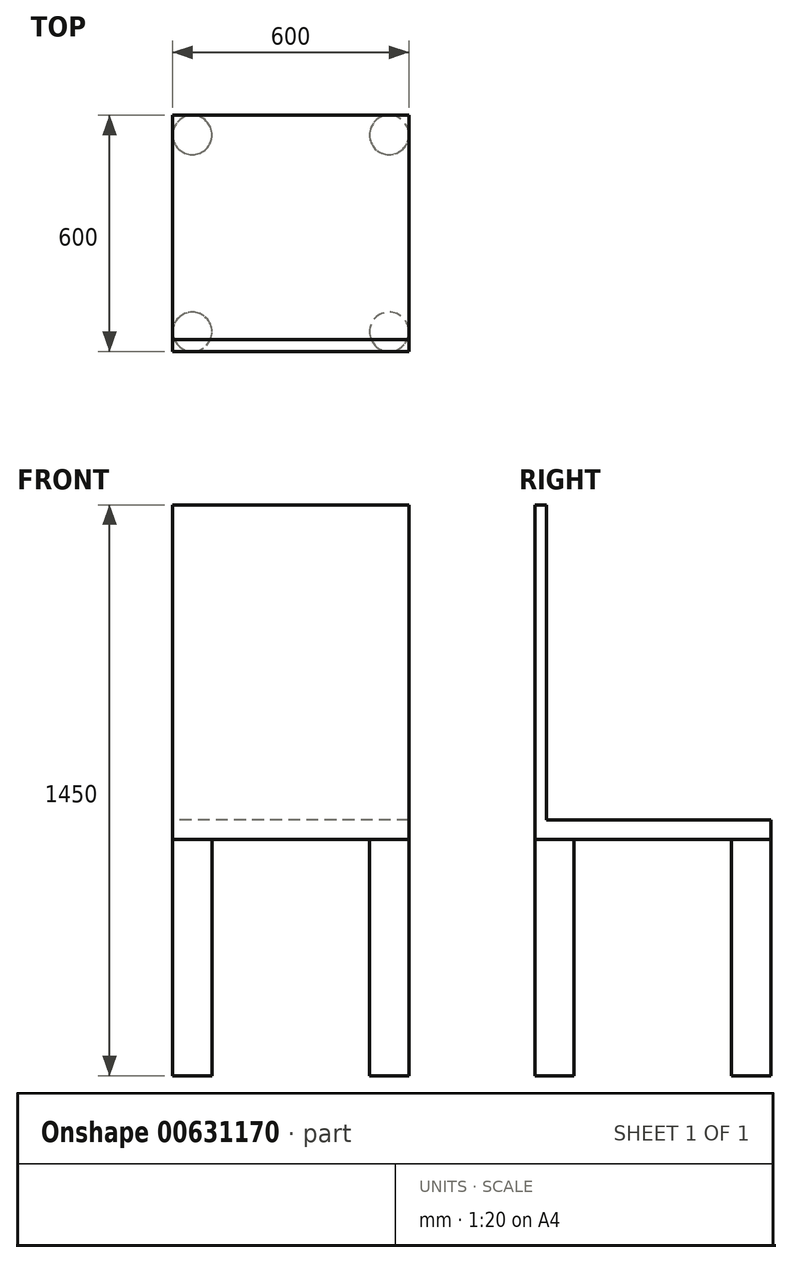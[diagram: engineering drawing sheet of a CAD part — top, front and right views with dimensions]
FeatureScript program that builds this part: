
annotation { "Feature Type Name" : "Feature", "Feature Type Description" : "" }
export const myFeature = defineFeature(function(context is Context, id is Id, definition is map)
    precondition{}
    {
        {
            var Q0;
            Q0=qCreatedBy(makeId("Top.planeOp"),FACE);
            var sketch = newSketch(context, id + "F0", { "sketchPlane" : qUnion([Q0])});
            skLineSegment(sketch, "E0.bottom", {"start": v(300, 300) * mm, "end": v(-300, 300) * mm});
            skLineSegment(sketch, "E0.top", {"start": v(300, -300) * mm, "end": v(-300, -300) * mm});
            skLineSegment(sketch, "E0.left", {"start": v(300, 300) * mm, "end": v(300, -300) * mm});
            skLineSegment(sketch, "E0.right", {"start": v(-300, 300) * mm, "end": v(-300, -300) * mm});
            skPoint(sketch, "E0.middle", {"position": v(0, 0) * mm});
            skSolve(sketch);
        }
        {
            var Q0;
            Q0=makeQuery(id+"F0.imprint","IMPRINT",FACE,{"disambiguationData":[TD([[makeQuery(id+"F0.imprint","IMPRINT",EDGE,{"derivedFrom":sQuery(id+"F0.wireOp",EDGE,"E0.bottom")}),1.0]])]});
            extrude(context, id + "F1", {"entities" : qUnion([Q0]), "depth" : 50 * mm, "offsetDistance" : 25.4 * mm});
        }
        {
            var Q0;
            Q0=makeQuery(id+"F1.opExtrude","CAP_FACE",FACE,{"disambiguationData":[OSD([sQuery(id+"F0.wireOp",EDGE,"E0.bottom"),sQuery(id+"F0.wireOp",EDGE,"E0.top"),sQuery(id+"F0.wireOp",EDGE,"E0.left"),sQuery(id+"F0.wireOp",EDGE,"E0.right")])],"isStart":false});
            var sketch = newSketch(context, id + "F2", { "sketchPlane" : qUnion([Q0])});
            skLineSegment(sketch, "E1.bottom", {"start": v(300, -300) * mm, "end": v(-300, -300) * mm});
            skLineSegment(sketch, "E1.top", {"start": v(300, -270) * mm, "end": v(-300, -270) * mm});
            skLineSegment(sketch, "E1.left", {"start": v(300, -300) * mm, "end": v(300, -270) * mm});
            skLineSegment(sketch, "E1.right", {"start": v(-300, -300) * mm, "end": v(-300, -270) * mm});
            skPoint(sketch, "E1.middle", {"position": v(0, -285) * mm});
            skPoint(sketch, "E1.middle.positionSnap0", {"position": v(0, -300) * mm});
            skPoint(sketch, "E1.centerSnap0", {"position": v(0, -300) * mm});
            skSolve(sketch);
        }
        {
            var Q0;
            Q0=makeQuery(id+"F2.imprint","IMPRINT",FACE,{"disambiguationData":[TD([[makeQuery(id+"F2.imprint","IMPRINT",EDGE,{"derivedFrom":sQuery(id+"F2.wireOp",EDGE,"E1.bottom")}),-1.0]])]});
            extrude(context, id + "F3", {"entities" : qUnion([Q0]), "operationType" : NewBodyOperationType.ADD, "depth" : 800 * mm, "offsetDistance" : 25.4 * mm});
        }
        {
            var Q0;
            Q0=makeQuery(id+"F1.opExtrude","CAP_FACE",FACE,{"disambiguationData":[OSD([sQuery(id+"F0.wireOp",EDGE,"E0.bottom"),sQuery(id+"F0.wireOp",EDGE,"E0.top"),sQuery(id+"F0.wireOp",EDGE,"E0.left"),sQuery(id+"F0.wireOp",EDGE,"E0.right")])],"isStart":true});
            var sketch = newSketch(context, id + "F4", { "sketchPlane" : qUnion([Q0])});
            skLineSegment(sketch, "E2.bottom", {"start": v(250, 250) * mm, "end": v(-250, 250) * mm});
            skLineSegment(sketch, "E2.top", {"start": v(250, -250) * mm, "end": v(-250, -250) * mm});
            skLineSegment(sketch, "E2.left", {"start": v(250, 250) * mm, "end": v(250, -250) * mm});
            skLineSegment(sketch, "E2.right", {"start": v(-250, 250) * mm, "end": v(-250, -250) * mm});
            skPoint(sketch, "E2.middle", {"position": v(0, 0) * mm});
            skCircle(sketch, "E3", {"center": v(-250, 250) * mm, "radius": 50 * mm});
            skCircle(sketch, "E4", {"center": v(250, 250) * mm, "radius": 50 * mm});
            skCircle(sketch, "E5", {"center": v(-250, -250) * mm, "radius": 50 * mm});
            skCircle(sketch, "E6", {"center": v(250, -250) * mm, "radius": 50 * mm});
            skSolve(sketch);
        }
        {
            var Q0;
            {var subQ3=sQuery(id+"F4.wireOp",EDGE,"E2.right");var subQ4=sQuery(id+"F4.wireOp",EDGE,"E2.bottom");var subQ5=makeQuery(id+"F4.imprint","INTERSECT",VERTEX,{"derivedFrom":[subQ4,subQ3]});Q0=makeQuery(id+"F4.imprint","IMPRINT",FACE,{"disambiguationData":[TD([[makeQuery(id+"F4.imprint","IMPRINT",EDGE,{"disambiguationData":[TD([[subQ5,1.0]])],"derivedFrom":subQ4}),-1.0]])]});}
            var Q1;
            {var subQ0=sQuery(id+"F4.wireOp",EDGE,"E2.right");var subQ1=sQuery(id+"F4.wireOp",EDGE,"E2.bottom");var subQ2=makeQuery(id+"F4.imprint","INTERSECT",VERTEX,{"derivedFrom":[subQ1,subQ0]});Q1=makeQuery(id+"F4.imprint","IMPRINT",FACE,{"disambiguationData":[TD([[makeQuery(id+"F4.imprint","IMPRINT",EDGE,{"disambiguationData":[TD([[subQ2,1.0]])],"derivedFrom":subQ1}),1.0]])]});}
            var Q2;
            {var subQ1=sQuery(id+"F4.wireOp",EDGE,"E2.bottom");var subQ4=sQuery(id+"F4.wireOp",EDGE,"E2.left");var subQ5=makeQuery(id+"F4.imprint","INTERSECT",VERTEX,{"derivedFrom":[subQ1,subQ4]});Q2=makeQuery(id+"F4.imprint","IMPRINT",FACE,{"disambiguationData":[TD([[makeQuery(id+"F4.imprint","IMPRINT",EDGE,{"disambiguationData":[TD([[subQ5,-1.0]])],"derivedFrom":subQ1}),-1.0]])]});}
            var Q3;
            {var subQ0=sQuery(id+"F4.wireOp",EDGE,"E2.right");var subQ1=sQuery(id+"F4.wireOp",EDGE,"E2.top");var subQ2=makeQuery(id+"F4.imprint","INTERSECT",VERTEX,{"derivedFrom":[subQ1,subQ0]});Q3=makeQuery(id+"F4.imprint","IMPRINT",FACE,{"disambiguationData":[TD([[makeQuery(id+"F4.imprint","IMPRINT",EDGE,{"disambiguationData":[TD([[subQ2,1.0]])],"derivedFrom":subQ1}),-1.0]])]});}
            var Q4;
            {var subQ3=sQuery(id+"F4.wireOp",EDGE,"E2.right");var subQ4=sQuery(id+"F4.wireOp",EDGE,"E2.top");var subQ5=makeQuery(id+"F4.imprint","INTERSECT",VERTEX,{"derivedFrom":[subQ4,subQ3]});Q4=makeQuery(id+"F4.imprint","IMPRINT",FACE,{"disambiguationData":[TD([[makeQuery(id+"F4.imprint","IMPRINT",EDGE,{"disambiguationData":[TD([[subQ5,1.0]])],"derivedFrom":subQ4}),1.0]])]});}
            var Q5;
            {var subQ0=sQuery(id+"F4.wireOp",EDGE,"E2.left");var subQ1=sQuery(id+"F4.wireOp",EDGE,"E2.top");var subQ2=makeQuery(id+"F4.imprint","INTERSECT",VERTEX,{"derivedFrom":[subQ1,subQ0]});Q5=makeQuery(id+"F4.imprint","IMPRINT",FACE,{"disambiguationData":[TD([[makeQuery(id+"F4.imprint","IMPRINT",EDGE,{"disambiguationData":[TD([[subQ2,-1.0]])],"derivedFrom":subQ1}),-1.0]])]});}
            var Q6;
            {var subQ1=sQuery(id+"F4.wireOp",EDGE,"E2.top");var subQ4=sQuery(id+"F4.wireOp",EDGE,"E2.left");var subQ7=makeQuery(id+"F4.imprint","INTERSECT",VERTEX,{"derivedFrom":[subQ1,subQ4]});Q6=makeQuery(id+"F4.imprint","IMPRINT",FACE,{"disambiguationData":[TD([[makeQuery(id+"F4.imprint","IMPRINT",EDGE,{"disambiguationData":[TD([[subQ7,-1.0]])],"derivedFrom":subQ1}),1.0]])]});}
            var Q7;
            {var subQ0=sQuery(id+"F4.wireOp",EDGE,"E2.left");var subQ1=sQuery(id+"F4.wireOp",EDGE,"E2.bottom");var subQ2=makeQuery(id+"F4.imprint","INTERSECT",VERTEX,{"derivedFrom":[subQ1,subQ0]});Q7=makeQuery(id+"F4.imprint","IMPRINT",FACE,{"disambiguationData":[TD([[makeQuery(id+"F4.imprint","IMPRINT",EDGE,{"disambiguationData":[TD([[subQ2,-1.0]])],"derivedFrom":subQ1}),1.0]])]});}
            extrude(context, id + "F5", {"entities" : qUnion([Q0, Q1, Q2, Q3, Q4, Q5, Q6, Q7]), "operationType" : NewBodyOperationType.ADD, "depth" : 600 * mm, "offsetDistance" : 25.4 * mm});
        }
    });
